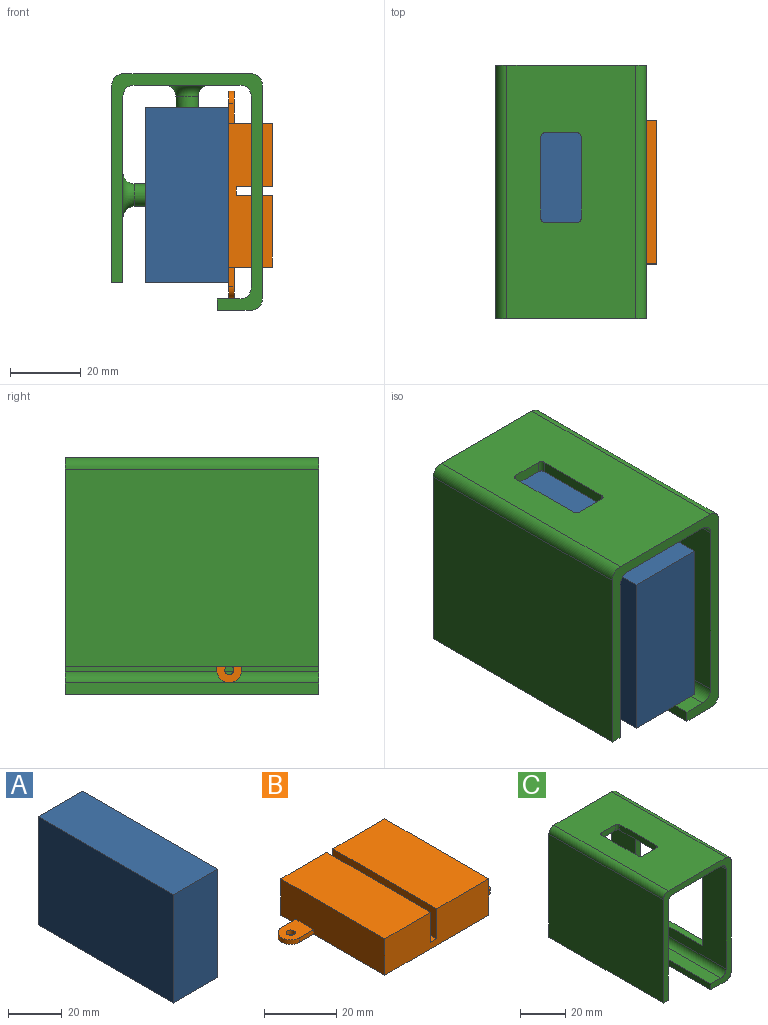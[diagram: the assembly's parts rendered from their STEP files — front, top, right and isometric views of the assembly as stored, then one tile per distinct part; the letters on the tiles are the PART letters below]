
ASSEMBLY  parts=3 mates=4
PART A: 6 faces, bbox 23.5x71.5x49.5 mm
  f0: plane 71.5x23.5mm, normal (0,0,-1), area 1679.9mm2, adj f1,f3,f4,f5
  f1: plane 71.5x49.53mm, normal (1,0,0), area 3541.4mm2, adj f0,f2,f4,f5
  f2: plane 71.5x23.5mm, normal (0,0,1), area 1679.9mm2, adj f1,f3,f4,f5
  f3: plane 71.5x49.53mm, normal (-1,0,0), area 3541.4mm2, adj f0,f2,f4,f5
  f4: plane 49.53x23.5mm, normal (0,-1,0), area 1163.7mm2, adj f0,f1,f2,f3
  f5: plane 49.53x23.5mm, normal (0,1,0), area 1163.7mm2, adj f0,f1,f2,f3
PART B: 20 faces, bbox 58.5x40.6x12.3 mm
  f0: plane 40.64x20.32mm, normal (0,0,1), area 825.8mm2, adj f1,f2,f3,f16
  f1: plane 40.64x12.32mm, normal (0,-1,0), area 476.7mm2, adj f0,f2,f4,f5,f6,f15,f16,f17
  f2: plane 40.64x12.32mm, normal (1,0,0), area 490mm2, adj f0,f1,f3,f6,f7,f8,f10
  f3: plane 40.64x12.32mm, normal (0,1,0), area 476.7mm2, adj f0,f2,f4,f5,f6,f15,f16,f17
  f4: plane 40.64x12.32mm, normal (-1,0,0), area 490mm2, adj f1,f3,f5,f6,f12,f13,f14
  f5: plane 40.64x17.96mm, normal (0,0,1), area 729.9mm2, adj f1,f3,f4,f15
  f6: plane 58.55x40.64mm, normal (0,0,-1), area 1756.1mm2, adj f1,f2,f3,f4,f7,f8,f9,f11
  f7: plane 5.4x1.52mm, normal (0,-1,0), area 8.2mm2, adj f2,f6,f9,f10
  f8: plane 5.4x1.52mm, normal (0,1,0), area 8.2mm2, adj f2,f6,f9,f10
  f9: cylinder r=3.49mm len=6.99mm, axis (0,0,-1), area 16.7mm2, adj f6,f7,f8,f10
  f10: plane 8.89x6.99mm, normal (0,0,1), area 51.8mm2, adj f2,f7,f8,f9,f19
  f11: cylinder r=3.49mm len=6.99mm, axis (0,0,-1), area 16.7mm2, adj f6,f12,f13,f14
  f12: plane 5.52x1.52mm, normal (0,1,0), area 8.4mm2, adj f4,f6,f11,f14
  f13: plane 5.52x1.52mm, normal (0,-1,0), area 8.4mm2, adj f4,f6,f11,f14
  f14: plane 9.02x6.99mm, normal (0,0,1), area 52.7mm2, adj f4,f11,f12,f13,f18
  f15: plane 40.64x10.16mm, normal (1,0,0), area 412.9mm2, adj f1,f3,f5,f17
  f16: plane 40.64x10.16mm, normal (-1,0,0), area 412.9mm2, adj f0,f1,f3,f17
  f17: plane 40.64x2.36mm, normal (0,0,1), area 95.9mm2, adj f1,f3,f15,f16
  f18: cylinder r=1.27mm len=2.54mm, axis (0,0,1), area 12.2mm2, adj f6,f14
  f19: cylinder r=1.27mm len=2.54mm, axis (0,0,1), area 12.2mm2, adj f6,f10
PART C: 36 faces, bbox 42.5x74.5x66.8 mm
  f0: plane 71.5x54.1mm, normal (-1,0,0), area 2111.9mm2, adj f10,f11,f18,f19,f20,f21,f26,f31
  f1: plane 71.5x60.45mm, normal (1,0,0), area 2565.9mm2, adj f10,f11,f18,f19,f20,f21,f27,f28
  f2: plane 71.5x36.2mm, normal (0,0,1), area 2299mm2, adj f10,f11,f14,f15,f16,f17,f28,f29
  f3: plane 71.5x29.85mm, normal (0,0,-1), area 1718.3mm2, adj f10,f11,f14,f15,f16,f17,f24,f30
  f4: plane 71.5x6.35mm, normal (0,0,1), area 454mm2, adj f5,f10,f11,f26
  f5: plane 71.5x3.18mm, normal (-1,0,0), area 227mm2, adj f4,f6,f10,f11
  f6: plane 71.5x9.53mm, normal (0,0,-1), area 681mm2, adj f5,f10,f11,f27
  f7: plane 71.5x55.88mm, normal (-1,0,0), area 3995.5mm2, adj f8,f10,f11,f29
  f8: plane 71.5x3.18mm, normal (0,0,-1), area 227mm2, adj f7,f9,f10,f11
  f9: plane 71.5x52.71mm, normal (1,0,0), area 3641.8mm2, adj f8,f10,f11,f25,f30
  f10: plane 66.8x42.55mm, normal (0,1,0), area 544.8mm2, adj f0,f1,f2,f3,f4,f5,f6,f7
  f11: plane 66.8x42.55mm, normal (0,-1,0), area 544.8mm2, adj f0,f1,f2,f3,f4,f5,f6,f7
  f12: cylinder r=3.17mm len=6.35mm, axis (-1,0,0), area 63.3mm2, adj f13,f25
  f13: plane 6.35x6.35mm, normal (1,0,0), area 31.7mm2, adj f12
  f14: plane 8.89x3.18mm, normal (0,1,0), area 28.2mm2, adj f2,f3,f32,f35
  f15: plane 22.86x3.18mm, normal (-1,0,0), area 72.6mm2, adj f2,f3,f32,f33
  f16: plane 8.89x3.18mm, normal (0,-1,0), area 28.2mm2, adj f2,f3,f33,f34
  f17: plane 22.86x3.18mm, normal (1,0,0), area 72.6mm2, adj f2,f3,f34,f35
  f18: plane 41.91x3.18mm, normal (0,0,1), area 133.1mm2, adj f0,f1,f19,f21
  f19: plane 41.91x3.18mm, normal (0,-1,0), area 133.1mm2, adj f0,f1,f18,f20
  f20: plane 41.91x3.18mm, normal (0,0,-1), area 133.1mm2, adj f0,f1,f19,f21
  f21: plane 41.91x3.18mm, normal (0,1,0), area 133.1mm2, adj f0,f1,f18,f20
  f22: cylinder r=3.17mm len=6.35mm, axis (0,0,1), area 63.3mm2, adj f23,f24
  f23: plane 6.35x6.35mm, normal (0,0,-1), area 31.7mm2, adj f22
  f24: torus R=6.35mm, axis (0,0,1), area 135.6mm2, adj f3,f22
  f25: torus R=6.35mm, axis (1,0,0), area 135.6mm2, adj f9,f12
  f26: cylinder r=3.17mm len=71.5mm, axis (0,-1,0), area 356.6mm2, adj f0,f4,f10,f11
  f27: cylinder r=3.17mm len=71.5mm, axis (0,-1,0), area 356.6mm2, adj f1,f6,f10,f11
  f28: cylinder r=3.17mm len=71.5mm, axis (0,1,0), area 356.6mm2, adj f1,f2,f10,f11
  f29: cylinder r=3.17mm len=71.5mm, axis (0,1,0), area 356.6mm2, adj f2,f7,f10,f11
  f30: cylinder r=3.17mm len=71.5mm, axis (0,-1,0), area 356.6mm2, adj f3,f9,f10,f11
  f31: cylinder r=3.17mm len=71.5mm, axis (0,1,0), area 356.6mm2, adj f0,f3,f10,f11
  f32: cylinder r=1.27mm len=3.18mm, axis (0,0,1), area 6.3mm2, adj f2,f3,f14,f15
  f33: cylinder r=1.27mm len=3.18mm, axis (0,0,-1), area 6.3mm2, adj f2,f3,f15,f16
  f34: cylinder r=1.27mm len=3.18mm, axis (0,0,1), area 6.3mm2, adj f2,f3,f16,f17
  f35: cylinder r=1.27mm len=3.18mm, axis (0,0,-1), area 6.3mm2, adj f2,f3,f14,f17
PLACE A t=(0,35.75,0)mm
PLACE B rot(axis=(0,1,0),90deg) t=(11.75,-0.02,-0.01)mm
PLACE C at identity fixed
MATE planar A.f0 <-> C.f8  axis (0,0,-1) through (0,0,-24.77)mm
MATE planar A.f1 <-> B.f6  axis (1,0,0) through (11.75,0,0)mm
MATE planar A.f3 <-> C.f12  axis (-1,0,0) through (-11.75,0,0)mm
MATE planar A.f4 <-> C.f11  axis (0,-1,0) through (0,-35.75,0)mm
